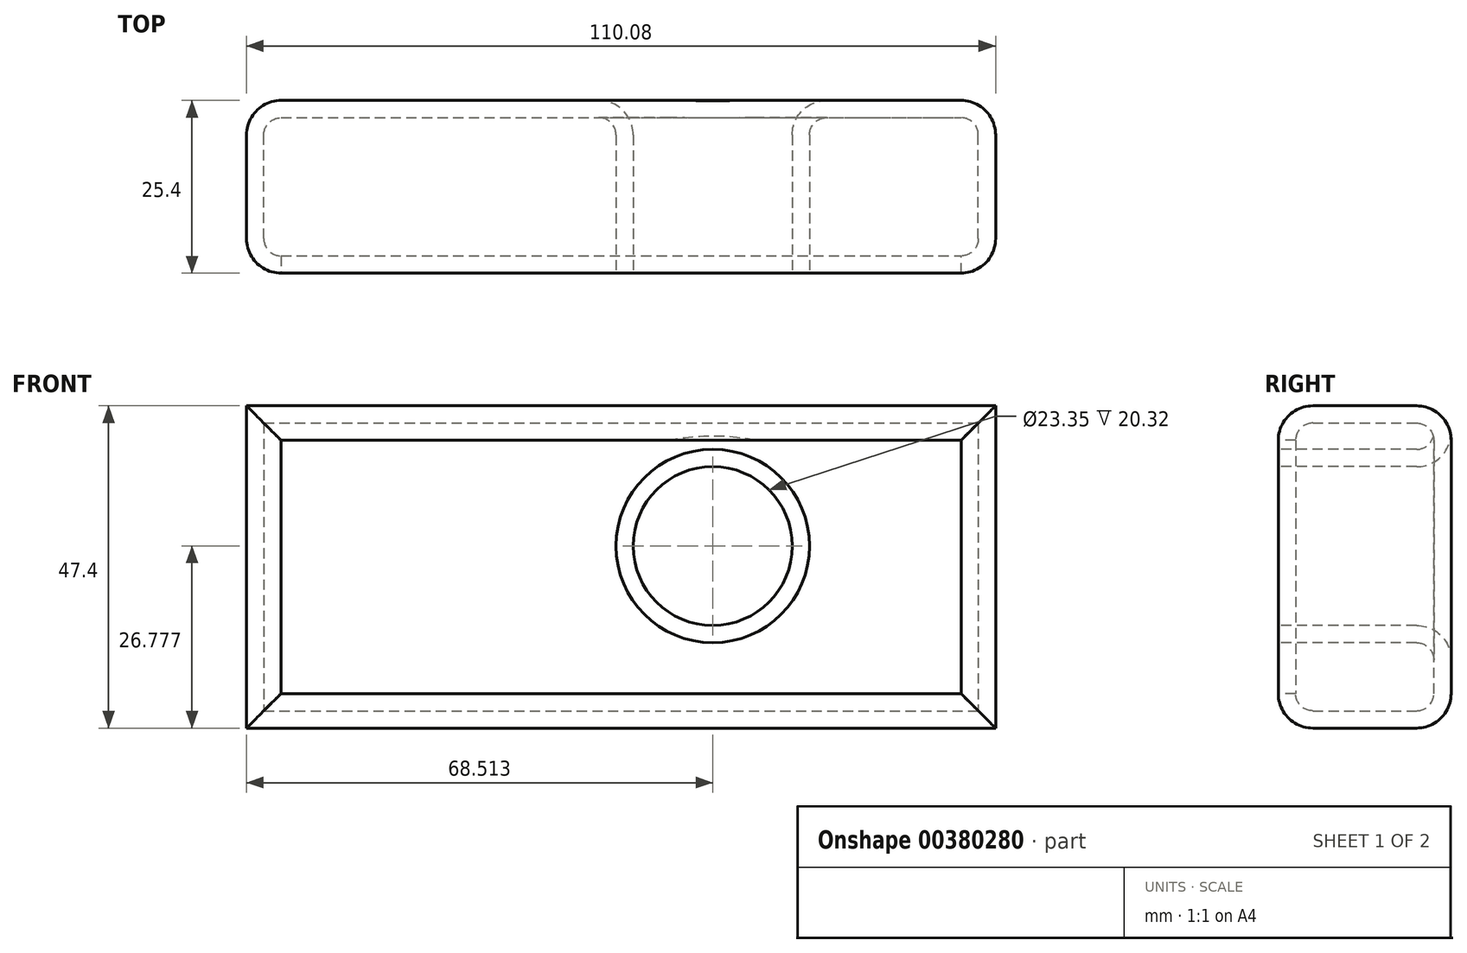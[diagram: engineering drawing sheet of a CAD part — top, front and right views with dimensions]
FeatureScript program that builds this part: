
annotation { "Feature Type Name" : "Feature", "Feature Type Description" : "" }
export const myFeature = defineFeature(function(context is Context, id is Id, definition is map)
    precondition{}
    {
        {
            var Q0;
            Q0=qCreatedBy(makeId("Front.planeOp"),FACE);
            var sketch = newSketch(context, id + "F0", { "sketchPlane" : qUnion([Q0])});
            skLineSegment(sketch, "E0.bottom", {"start": v(-55.04, 23.7) * mm, "end": v(55.04, 23.7) * mm});
            skLineSegment(sketch, "E0.top", {"start": v(-55.04, -23.7) * mm, "end": v(55.04, -23.7) * mm});
            skLineSegment(sketch, "E0.left", {"start": v(-55.04, 23.7) * mm, "end": v(-55.04, -23.7) * mm});
            skLineSegment(sketch, "E0.right", {"start": v(55.04, 23.7) * mm, "end": v(55.04, -23.7) * mm});
            skPoint(sketch, "E0.middle", {"position": v(0, 0) * mm});
            skSolve(sketch);
        }
        {
            var Q0;
            Q0=qSketchRegion(id+"F0",true);
            extrude(context, id + "F1", {"entities" : qUnion([Q0]), "depth" : 25.4 * mm});
        }
        {
            var Q0;
            Q0=makeQuery(id+"F1.opExtrude","CAP_FACE",FACE,{"disambiguationData":[OSD([sQuery(id+"F0.wireOp",EDGE,"E0.bottom"),sQuery(id+"F0.wireOp",EDGE,"E0.top"),sQuery(id+"F0.wireOp",EDGE,"E0.left"),sQuery(id+"F0.wireOp",EDGE,"E0.right")])],"isStart":false});
            var sketch = newSketch(context, id + "F2", { "sketchPlane" : qUnion([Q0])});
            skCircle(sketch, "E1", {"center": v(13.47, 3.08) * mm, "radius": 11.67 * mm});
            skSolve(sketch);
        }
        {
            var Q0;
            Q0=makeQuery(id+"F2.imprint","IMPRINT",FACE,{"disambiguationData":[TD([[makeQuery(id+"F2.imprint","IMPRINT",EDGE,{"derivedFrom":sQuery(id+"F2.wireOp",EDGE,"E1")}),1.0]])]});
            extrude(context, id + "F3", {"entities" : qUnion([Q0]), "operationType" : NewBodyOperationType.REMOVE, "endBound" : BoundingType.THROUGH_ALL, "oppositeDirection" : true, "depth" : 25.4 * mm});
        }
        {
            var Q0;
            Q0=makeQuery(id+"F3.boolean.opBoolean","COPY",EDGE,{"derivedFrom":makeQuery(id+"F3.opExtrude","CAP_EDGE",EDGE,{"disambiguationData":[OSD([sQuery(id+"F2.wireOp",EDGE,"E1")])],"isStart":true})});
            var Q1;
            Q1=makeQuery(id+"F3.boolean.opBoolean","INTERSECT",EDGE,{"derivedFrom":[makeQuery(id+"F1.opExtrude","CAP_FACE",FACE,{"disambiguationData":[OSD([sQuery(id+"F0.wireOp",EDGE,"E0.bottom"),sQuery(id+"F0.wireOp",EDGE,"E0.top"),sQuery(id+"F0.wireOp",EDGE,"E0.left"),sQuery(id+"F0.wireOp",EDGE,"E0.right")])],"isStart":true}),makeQuery(id+"F3.opExtrude","SWEPT_FACE",FACE,{"disambiguationData":[OSD([sQuery(id+"F2.wireOp",EDGE,"E1")])]})]});
            var Q2;
            Q2=makeQuery(id+"F1.opExtrude","CAP_EDGE",EDGE,{"disambiguationData":[OSD([sQuery(id+"F0.wireOp",EDGE,"E0.bottom")])],"isStart":true});
            var Q3;
            Q3=makeQuery(id+"F1.opExtrude","CAP_EDGE",EDGE,{"disambiguationData":[OSD([sQuery(id+"F0.wireOp",EDGE,"E0.right")])],"isStart":true});
            var Q4;
            Q4=makeQuery(id+"F1.opExtrude","CAP_EDGE",EDGE,{"disambiguationData":[OSD([sQuery(id+"F0.wireOp",EDGE,"E0.top")])],"isStart":true});
            var Q5;
            Q5=makeQuery(id+"F1.opExtrude","CAP_FACE",FACE,{"disambiguationData":[OSD([sQuery(id+"F0.wireOp",EDGE,"E0.bottom"),sQuery(id+"F0.wireOp",EDGE,"E0.top"),sQuery(id+"F0.wireOp",EDGE,"E0.left"),sQuery(id+"F0.wireOp",EDGE,"E0.right")])],"isStart":true});
            fillet(context, id + "F4", {"entities" : qUnion([Q0, Q1, Q2, Q3, Q4, Q5]), "radius" : 5.08 * mm, "tangentPropagation" : true, "allowEdgeOverflow" : false});
        }
        {
            var Q0;
            Q0=makeQuery(id+"F1.opExtrude","CAP_EDGE",EDGE,{"disambiguationData":[OSD([sQuery(id+"F0.wireOp",EDGE,"E0.bottom")])],"isStart":false});
            var Q1;
            Q1=makeQuery(id+"F1.opExtrude","CAP_EDGE",EDGE,{"disambiguationData":[OSD([sQuery(id+"F0.wireOp",EDGE,"E0.top")])],"isStart":false});
            var Q2;
            Q2=makeQuery(id+"F1.opExtrude","CAP_EDGE",EDGE,{"disambiguationData":[OSD([sQuery(id+"F0.wireOp",EDGE,"E0.left")])],"isStart":false});
            var Q3;
            Q3=makeQuery(id+"F1.opExtrude","CAP_EDGE",EDGE,{"disambiguationData":[OSD([sQuery(id+"F0.wireOp",EDGE,"E0.right")])],"isStart":false});
            fillet(context, id + "F5", {"entities" : qUnion([Q0, Q1, Q2, Q3]), "radius" : 5.08 * mm, "tangentPropagation" : true, "allowEdgeOverflow" : false});
        }
        {
            var Q0;
            Q0=makeQuery(id+"F1.opExtrude","CAP_FACE",FACE,{"disambiguationData":[OSD([sQuery(id+"F0.wireOp",EDGE,"E0.bottom"),sQuery(id+"F0.wireOp",EDGE,"E0.top"),sQuery(id+"F0.wireOp",EDGE,"E0.left"),sQuery(id+"F0.wireOp",EDGE,"E0.right")])],"isStart":false});
            shell(context, id + "F6", {"entities" : qUnion([Q0]), "thickness" : 2.54 * mm});
        }
    });
